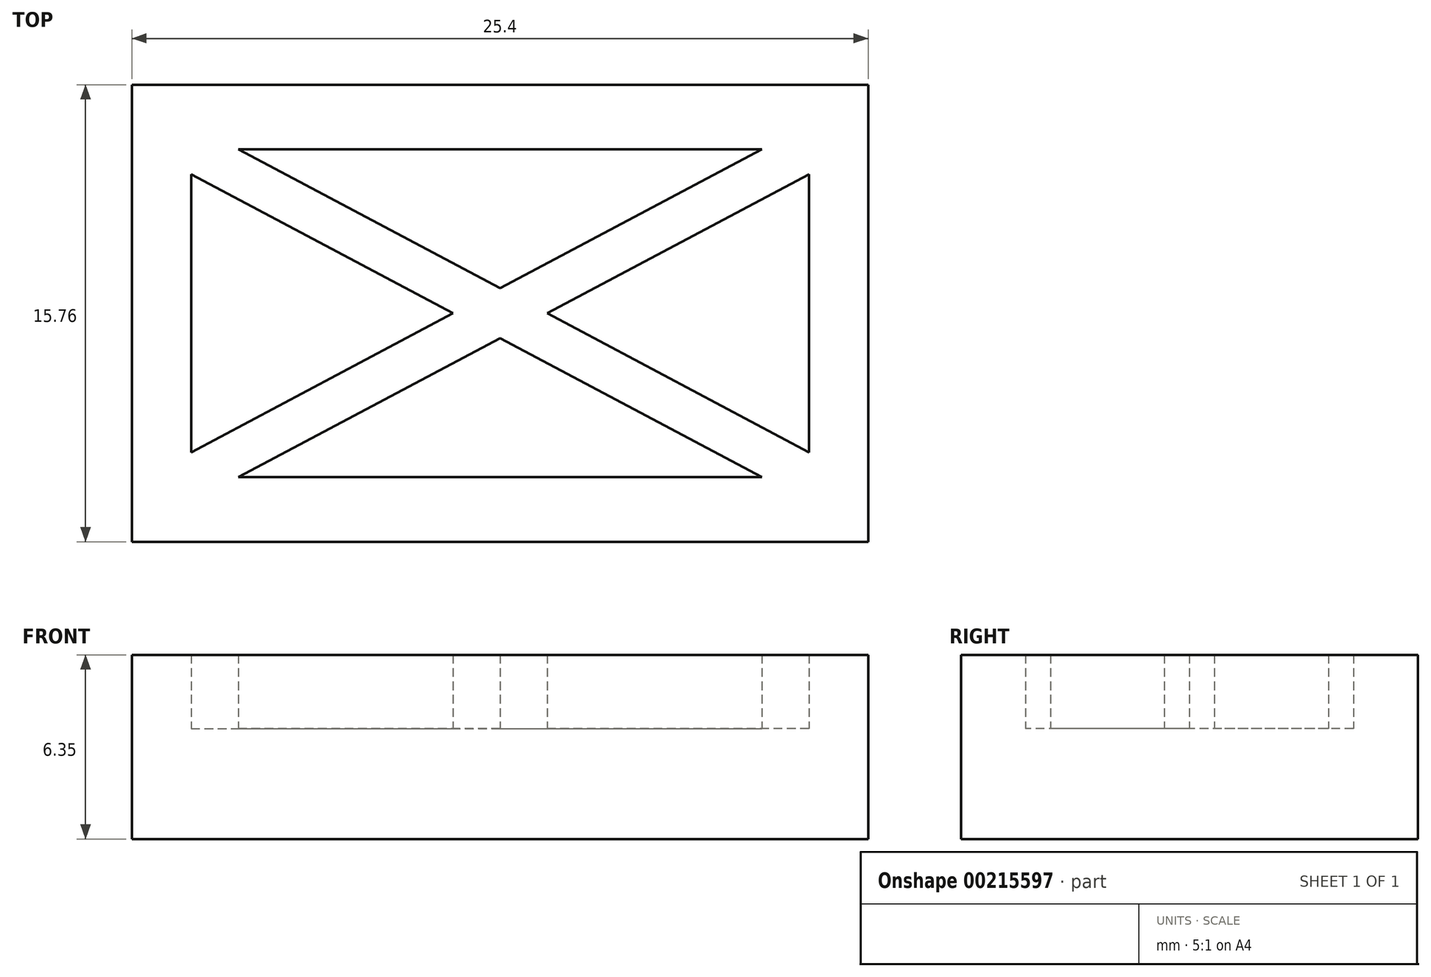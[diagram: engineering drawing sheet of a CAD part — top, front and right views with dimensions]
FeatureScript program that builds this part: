
annotation { "Feature Type Name" : "Feature", "Feature Type Description" : "" }
export const myFeature = defineFeature(function(context is Context, id is Id, definition is map)
    precondition{}
    {
        {
            var Q0;
            Q0=qCreatedBy(makeId("Top.planeOp"),FACE);
            var sketch = newSketch(context, id + "F0", { "sketchPlane" : qUnion([Q0])});
            skLineSegment(sketch, "E0.bottom", {"start": v(-12.7, 7.88) * mm, "end": v(12.7, 7.88) * mm});
            skLineSegment(sketch, "E0.top", {"start": v(-12.7, -7.88) * mm, "end": v(12.7, -7.88) * mm});
            skLineSegment(sketch, "E0.left", {"start": v(-12.7, 7.88) * mm, "end": v(-12.7, -7.88) * mm});
            skLineSegment(sketch, "E0.right", {"start": v(12.7, 7.88) * mm, "end": v(12.7, -7.88) * mm});
            skPoint(sketch, "E0.middle", {"position": v(0, 0) * mm});
            skLineSegment(sketch, "E1.bottom", {"start": v(-9.03, 5.66) * mm, "end": v(9.03, 5.66) * mm});
            skLineSegment(sketch, "E1.top", {"start": v(-9.03, -5.66) * mm, "end": v(9.03, -5.66) * mm});
            skLineSegment(sketch, "E1.left", {"start": v(-10.65, 4.8) * mm, "end": v(-10.65, -4.8) * mm});
            skLineSegment(sketch, "E1.right", {"start": v(10.65, 4.8) * mm, "end": v(10.65, -4.8) * mm});
            skLineSegment(sketch, "E2.0", {"start": v(-10.65, 4.8) * mm, "end": v(-1.63, 0) * mm});
            skLineSegment(sketch, "E3.0", {"start": v(-9.03, 5.66) * mm, "end": v(0, 0.86) * mm});
            skLineSegment(sketch, "E4.0", {"start": v(9.03, 5.66) * mm, "end": v(0, 0.86) * mm});
            skLineSegment(sketch, "E5.0", {"start": v(10.65, 4.8) * mm, "end": v(1.63, 0) * mm});
            skLineSegment(sketch, "E6.trimOffspring", {"start": v(0, -0.86) * mm, "end": v(-9.03, -5.66) * mm});
            skLineSegment(sketch, "E7.trimOffspring", {"start": v(0, -0.86) * mm, "end": v(9.03, -5.66) * mm});
            skLineSegment(sketch, "E8.trimOffspring", {"start": v(1.63, 0) * mm, "end": v(10.65, -4.8) * mm});
            skLineSegment(sketch, "E9.trimOffspring", {"start": v(-1.63, 0) * mm, "end": v(-11.01, -4.98) * mm});
            skPoint(sketch, "E10.orphan", {"position": v(10.65, 5.66) * mm});
            skPoint(sketch, "E11.orphan", {"position": v(10.65, -5.66) * mm});
            skPoint(sketch, "E12.orphan", {"position": v(-10.65, -5.66) * mm});
            skPoint(sketch, "E13.orphan", {"position": v(-10.65, 5.66) * mm});
            skSolve(sketch);
        }
        {
            var Q0;
            Q0=makeQuery(id+"F0.imprint","IMPRINT",FACE,{"disambiguationData":[TD([[makeQuery(id+"F0.imprint","IMPRINT",EDGE,{"derivedFrom":sQuery(id+"F0.wireOp",EDGE,"E0.bottom")}),-1.0]])]});
            extrude(context, id + "F1", {"entities" : qUnion([Q0]), "depth" : 6.35 * mm});
        }
        {
            var Q0;
            Q0=makeQuery(id+"F0.imprint","IMPRINT",FACE,{"disambiguationData":[TD([[makeQuery(id+"F0.imprint","IMPRINT",EDGE,{"derivedFrom":sQuery(id+"F0.wireOp",EDGE,"E1.bottom")}),-1.0]])]});
            var Q1;
            {var subQ0=sQuery(id+"F0.wireOp",EDGE,"E1.left");Q1=makeQuery(id+"F0.imprint","IMPRINT",FACE,{"disambiguationData":[TD([[makeQuery(id+"F0.imprint","IMPRINT",EDGE,{"derivedFrom":subQ0}),1.0]])]});}
            var Q2;
            Q2=makeQuery(id+"F0.imprint","IMPRINT",FACE,{"disambiguationData":[TD([[makeQuery(id+"F0.imprint","IMPRINT",EDGE,{"derivedFrom":sQuery(id+"F0.wireOp",EDGE,"E1.top")}),1.0]])]});
            var Q3;
            Q3=makeQuery(id+"F0.imprint","IMPRINT",FACE,{"disambiguationData":[TD([[makeQuery(id+"F0.imprint","IMPRINT",EDGE,{"derivedFrom":sQuery(id+"F0.wireOp",EDGE,"E1.right")}),-1.0]])]});
            extrude(context, id + "F2", {"entities" : qUnion([Q0, Q1, Q2, Q3]), "operationType" : NewBodyOperationType.ADD, "depth" : 3.8 * mm});
        }
    });
